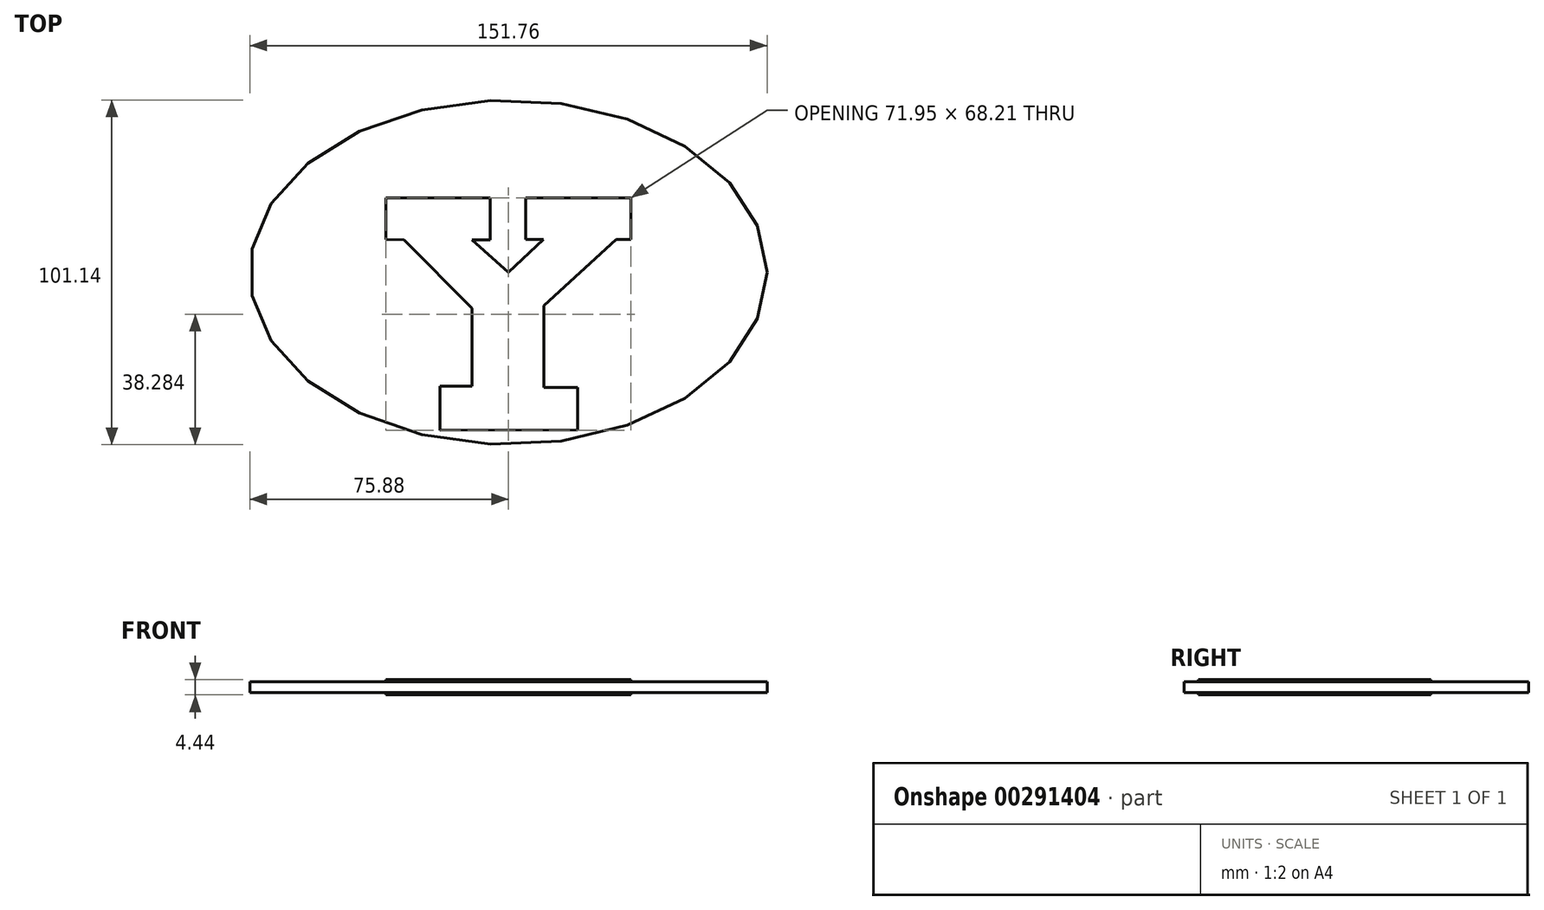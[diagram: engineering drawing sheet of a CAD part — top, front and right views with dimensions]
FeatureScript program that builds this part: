
annotation { "Feature Type Name" : "Feature", "Feature Type Description" : "" }
export const myFeature = defineFeature(function(context is Context, id is Id, definition is map)
    precondition{}
    {
        {
            var Q0;
            Q0=qCreatedBy(makeId("Top.planeOp"),FACE);
            var sketch = newSketch(context, id + "F0", { "sketchPlane" : qUnion([Q0])});
            skEllipse(sketch, "E0", {"center": v(0, 0) * mm, "majorRadius": 75.88 * mm, "minorRadius": 50.57 * mm, "majorAxis": v(1, 0)});
            skLineSegment(sketch, "E1", {"start": v(-5.3, 17.5) * mm, "end": v(-5.3, 9.44) * mm});
            skLineSegment(sketch, "E2", {"start": v(-5.3, 9.44) * mm, "end": v(-10.62, 9.44) * mm});
            skLineSegment(sketch, "E3", {"start": v(-10.62, 9.44) * mm, "end": v(0, 0) * mm});
            skLineSegment(sketch, "E4", {"start": v(5.11, 17.3) * mm, "end": v(5.11, 9.63) * mm});
            skLineSegment(sketch, "E5", {"start": v(5.11, 9.63) * mm, "end": v(10.22, 9.63) * mm});
            skLineSegment(sketch, "E6", {"start": v(10.22, 9.63) * mm, "end": v(0, 0) * mm});
            skLineSegment(sketch, "E7", {"start": v(-5.3, 17.5) * mm, "end": v(-5.3, 21.82) * mm});
            skLineSegment(sketch, "E8", {"start": v(5.11, 17.3) * mm, "end": v(5.11, 21.82) * mm});
            skLineSegment(sketch, "E9", {"start": v(5.11, 21.82) * mm, "end": v(35.98, 21.82) * mm});
            skLineSegment(sketch, "E10", {"start": v(35.98, 21.82) * mm, "end": v(35.98, 9.63) * mm});
            skLineSegment(sketch, "E11", {"start": v(35.98, 9.63) * mm, "end": v(31.65, 9.63) * mm});
            skLineSegment(sketch, "E12", {"start": v(31.65, 9.63) * mm, "end": v(10.42, -9.83) * mm});
            skLineSegment(sketch, "E13", {"start": v(-5.3, 21.82) * mm, "end": v(-35.98, 21.82) * mm});
            skLineSegment(sketch, "E14", {"start": v(-35.98, 21.82) * mm, "end": v(-35.98, 9.63) * mm});
            skLineSegment(sketch, "E15", {"start": v(-35.98, 9.63) * mm, "end": v(-30.67, 9.44) * mm});
            skLineSegment(sketch, "E16", {"start": v(-30.67, 9.44) * mm, "end": v(-10.62, -10.62) * mm});
            skLineSegment(sketch, "E17", {"start": v(-10.62, -10.62) * mm, "end": v(-10.62, -33.42) * mm});
            skLineSegment(sketch, "E18", {"start": v(10.42, -9.83) * mm, "end": v(10.42, -33.81) * mm});
            skLineSegment(sketch, "E19", {"start": v(10.42, -33.81) * mm, "end": v(20.25, -33.81) * mm});
            skLineSegment(sketch, "E20", {"start": v(20.25, -33.81) * mm, "end": v(20.25, -46.2) * mm});
            skLineSegment(sketch, "E21", {"start": v(-10.62, -33.42) * mm, "end": v(-20.05, -33.42) * mm});
            skLineSegment(sketch, "E22", {"start": v(-20.05, -33.42) * mm, "end": v(-20.05, -46.4) * mm});
            skLineSegment(sketch, "E23", {"start": v(-20.05, -46.4) * mm, "end": v(20.25, -46.2) * mm});
            skSolve(sketch);
        }
        {
            var Q0;
            Q0=makeQuery(id+"F0.imprint","IMPRINT",FACE,{"disambiguationData":[TD([[makeQuery(id+"F0.imprint","IMPRINT",EDGE,{"derivedFrom":sQuery(id+"F0.wireOp",EDGE,"E1")}),-1.0]])]});
            var sketch = newSketch(context, id + "F1", { "sketchPlane" : qUnion([Q0])});
            skSolve(sketch);
        }
        {
            var Q0;
            Q0=makeQuery(id+"F0.imprint","IMPRINT",FACE,{"disambiguationData":[TD([[makeQuery(id+"F0.imprint","IMPRINT",EDGE,{"derivedFrom":sQuery(id+"F0.wireOp",EDGE,"E0")}),1.0]])]});
            extrude(context, id + "F2", {"entities" : qUnion([Q0]), "endBound" : BoundingType.SYMMETRIC, "depth" : 3.17 * mm});
        }
        {
            var Q0;
            Q0=makeQuery(id+"F1.imprint","IMPRINT",FACE,{"disambiguationData":[TD([[makeQuery(id+"F1.imprint","IMPRINT",EDGE,{"derivedFrom":makeQuery(id+"F0.imprint","IMPRINT",EDGE,{"derivedFrom":sQuery(id+"F0.wireOp",EDGE,"E1")})}),-1.0]])]});
            extrude(context, id + "F3", {"entities" : qUnion([Q0]), "operationType" : NewBodyOperationType.ADD, "endBound" : BoundingType.SYMMETRIC, "depth" : 4.44 * mm});
        }
    });
